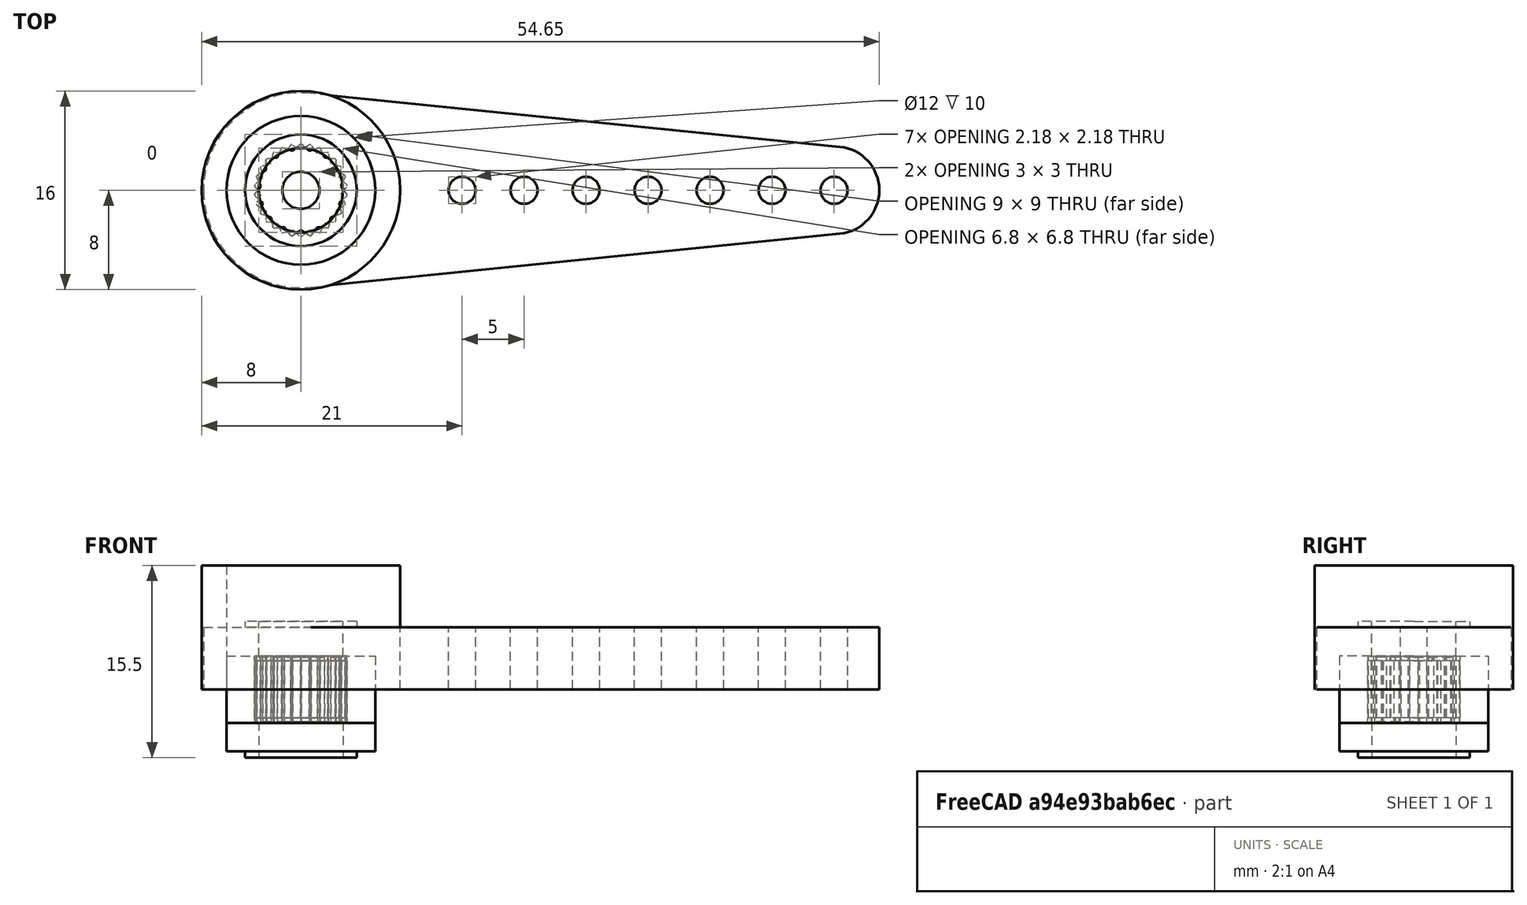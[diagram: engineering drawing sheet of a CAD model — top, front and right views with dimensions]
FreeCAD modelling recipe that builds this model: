
FCSTD DOCUMENT  (FreeCAD 0.19R24276 (Git))
Label: my_horn
License: All rights reserved
LicenseURL: http://en.wikipedia.org/wiki/All_rights_reserved
objects: App::Part×2, Part::Feature×1, Sketcher::SketchObject×1, PartDesign::Pad×1, PartDesign::Body×1, Part::Cut×1, Part::FeaturePython×1, App::DocumentObjectGroup×1
note: 7 computed .brp shape members not serialized (recipe doc carries the construction recipe); baked Part::Feature solids carry a one-line shape summary decoded from their .brp

FEATURE [Part::Feature] Part__Feature  label="HS-805 Servo Horn B"
  shape: bbox 54.5 x 15.7 x 8.2 mm, 78 faces (baked)
FEATURE [App::Part] Part
  Group = -> [Part__Feature]
  Origin = -> Origin
  Placement = pos=(0,0,0) rot=(-1,0,0;3.14159rad)
FEATURE [Sketcher::SketchObject] Sketch
  FullyConstrained = false
  MapMode = 5
  Support = -> [XY_Plane002]
  sketch-geometry (2):
    g0: Circle CenterX=0 CenterY=0 CenterZ=0 NormalX=0 NormalY=0 NormalZ=1 AngleXU=0 Radius=6
    g1: Circle CenterX=0 CenterY=0 CenterZ=0 NormalX=0 NormalY=0 NormalZ=1 AngleXU=0 Radius=8
  constraints (2):
    c: PointOnObject(g0,g-1)
    c: Coincident(g1,g0)
FEATURE [PartDesign::Pad] Pad
  Direction = (1,1,1)
  Length = 10
  Length2 = 100
  Profile = -> Sketch
  Type = 0
FEATURE [PartDesign::Body] Body
  Group = -> [Sketch,Pad]
  Origin = -> Origin002
  Tip = -> Pad
FEATURE [App::Part] Part001
  Group = -> [Body]
  Origin = -> Origin001
  Placement = pos=(0,0,-5) rot=(0,0,1;0rad)
FEATURE [Part::Cut] Cut
  Base = -> Part
  Tool = -> Part001
FEATURE [Part::FeaturePython] Cut_child1  label="Cut.1"  # WARN: FeaturePython — macro-defined, semantics opaque (R4)
  Base = -> Cut
  FilterType = 1
  Invert = false
  OverrideMaxVal = 0
  WindowFrom = 80
  WindowTo = 100
  items = 1
FEATURE [App::DocumentObjectGroup] GrExplode_Cut  label="Exploded Cut"
  Group = -> [Cut_child1]
